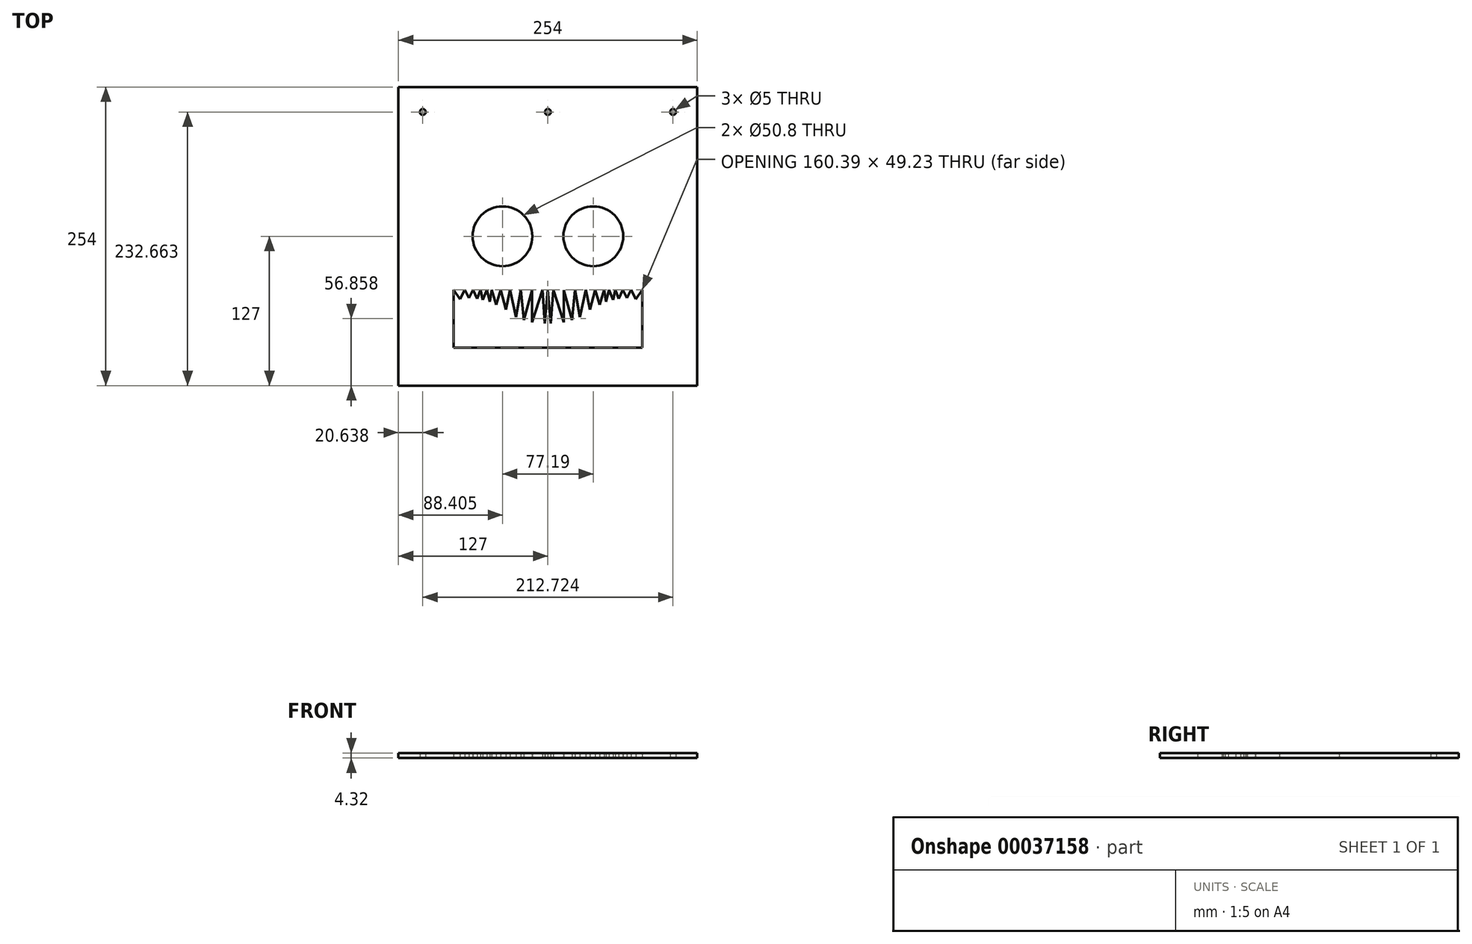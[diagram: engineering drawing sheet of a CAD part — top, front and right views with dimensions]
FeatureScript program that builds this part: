
annotation { "Feature Type Name" : "Feature", "Feature Type Description" : "" }
export const myFeature = defineFeature(function(context is Context, id is Id, definition is map)
    precondition{}
    {
        {
            var Q0;
            Q0=qCreatedBy(makeId("Top.planeOp"),FACE);
            var sketch = newSketch(context, id + "F0", { "sketchPlane" : qUnion([Q0])});
            skLineSegment(sketch, "E0.rect.bottom", {"start": v(127, 127) * mm, "end": v(-127, 127) * mm});
            skLineSegment(sketch, "E0.rect.top", {"start": v(127, -127) * mm, "end": v(-127, -127) * mm});
            skLineSegment(sketch, "E0.rect.left", {"start": v(127, 127) * mm, "end": v(127, -127) * mm});
            skLineSegment(sketch, "E0.rect.right", {"start": v(-127, 127) * mm, "end": v(-127, -127) * mm});
            skPoint(sketch, "E0.rect.middle", {"position": v(0, 0) * mm});
            skPoint(sketch, "E1.endSnap0", {"position": v(0, 127) * mm});
            skCircle(sketch, "E2", {"center": v(0, 105.66) * mm, "radius": 2.5 * mm});
            skCircle(sketch, "E3.MirrorC", {"center": v(-106.36, 105.66) * mm, "radius": 2.5 * mm});
            skCircle(sketch, "E4.MirrorC", {"center": v(106.36, 105.66) * mm, "radius": 2.5 * mm});
            skCircle(sketch, "E5", {"center": v(-38.6, 0) * mm, "radius": 25.4 * mm});
            skCircle(sketch, "E6.MirrorC", {"center": v(38.6, 0) * mm, "radius": 25.4 * mm});
            skLineSegment(sketch, "E7.top", {"start": v(0, -94.75) * mm, "end": v(-80.2, -94.75) * mm});
            skLineSegment(sketch, "E7.left", {"start": v(0, -45.53) * mm, "end": v(0, -94.75) * mm});
            skLineSegment(sketch, "E7.right", {"start": v(-80.2, -45.53) * mm, "end": v(-80.2, -94.75) * mm});
            skLineSegment(sketch, "E8.MirrorCS", {"start": v(80.2, -45.53) * mm, "end": v(80.2, -94.75) * mm});
            skLineSegment(sketch, "E9.MirrorCS", {"start": v(0, -94.75) * mm, "end": v(80.2, -94.75) * mm});
            skLineSegment(sketch, "E10", {"start": v(-80.2, -45.53) * mm, "end": v(-74.65, -53.39) * mm});
            skLineSegment(sketch, "E11", {"start": v(-74.65, -53.39) * mm, "end": v(-70.72, -45.53) * mm});
            skLineSegment(sketch, "E12", {"start": v(-70.72, -45.53) * mm, "end": v(-67.25, -52.7) * mm});
            skLineSegment(sketch, "E13", {"start": v(-67.25, -52.7) * mm, "end": v(-63.79, -45.53) * mm});
            skLineSegment(sketch, "E14", {"start": v(-63.79, -45.53) * mm, "end": v(-60.09, -53.16) * mm});
            skLineSegment(sketch, "E15", {"start": v(-60.09, -53.16) * mm, "end": v(-57.32, -45.53) * mm});
            skLineSegment(sketch, "E16", {"start": v(-57.32, -45.53) * mm, "end": v(-55.47, -54.08) * mm});
            skLineSegment(sketch, "E17", {"start": v(-55.47, -54.08) * mm, "end": v(-51.77, -45.53) * mm});
            skLineSegment(sketch, "E18", {"start": v(-51.77, -45.53) * mm, "end": v(-49.46, -55.7) * mm});
            skLineSegment(sketch, "E19", {"start": v(-49.46, -55.7) * mm, "end": v(-47.84, -45.53) * mm});
            skLineSegment(sketch, "E20", {"start": v(-47.84, -45.53) * mm, "end": v(-43.91, -58.24) * mm});
            skLineSegment(sketch, "E21", {"start": v(-43.91, -58.24) * mm, "end": v(-40.1, -45.53) * mm});
            skLineSegment(sketch, "E22", {"start": v(-40.1, -45.53) * mm, "end": v(-35.6, -62.4) * mm});
            skLineSegment(sketch, "E23", {"start": v(-35.6, -62.4) * mm, "end": v(-32.36, -45.53) * mm});
            skLineSegment(sketch, "E24", {"start": v(-32.36, -45.53) * mm, "end": v(-27.27, -68.87) * mm});
            skLineSegment(sketch, "E25", {"start": v(-27.27, -68.87) * mm, "end": v(-23.11, -45.53) * mm});
            skLineSegment(sketch, "E26", {"start": v(-23.11, -45.53) * mm, "end": v(-20.57, -71.18) * mm});
            skLineSegment(sketch, "E27", {"start": v(-20.57, -71.18) * mm, "end": v(-13.4, -45.76) * mm});
            skLineSegment(sketch, "E28", {"start": v(-13.4, -45.76) * mm, "end": v(-13.4, -73.03) * mm});
            skLineSegment(sketch, "E29", {"start": v(-13.4, -73.03) * mm, "end": v(-4.62, -45.53) * mm});
            skLineSegment(sketch, "E30", {"start": v(-4.62, -45.53) * mm, "end": v(-2.54, -74.19) * mm});
            skLineSegment(sketch, "E31", {"start": v(-2.54, -74.19) * mm, "end": v(0, -45.53) * mm});
            skLineSegment(sketch, "E32.MirrorCS", {"start": v(2.54, -74.19) * mm, "end": v(0, -45.53) * mm});
            skLineSegment(sketch, "E33.MirrorCS", {"start": v(4.62, -45.53) * mm, "end": v(2.54, -74.19) * mm});
            skLineSegment(sketch, "E34.MirrorCS", {"start": v(13.4, -73.03) * mm, "end": v(4.62, -45.53) * mm});
            skLineSegment(sketch, "E35.MirrorCS", {"start": v(13.4, -45.76) * mm, "end": v(13.4, -73.03) * mm});
            skLineSegment(sketch, "E36.MirrorCS", {"start": v(20.57, -71.18) * mm, "end": v(13.4, -45.76) * mm});
            skLineSegment(sketch, "E37.MirrorCS", {"start": v(23.11, -45.53) * mm, "end": v(20.57, -71.18) * mm});
            skLineSegment(sketch, "E38.MirrorCS", {"start": v(27.27, -68.87) * mm, "end": v(23.11, -45.53) * mm});
            skLineSegment(sketch, "E39.MirrorCS", {"start": v(32.36, -45.53) * mm, "end": v(27.27, -68.87) * mm});
            skLineSegment(sketch, "E40.MirrorCS", {"start": v(35.6, -62.4) * mm, "end": v(32.36, -45.53) * mm});
            skLineSegment(sketch, "E41.MirrorCS", {"start": v(40.1, -45.53) * mm, "end": v(35.6, -62.4) * mm});
            skLineSegment(sketch, "E42.MirrorCS", {"start": v(43.91, -58.24) * mm, "end": v(40.1, -45.53) * mm});
            skLineSegment(sketch, "E43.MirrorCS", {"start": v(47.84, -45.53) * mm, "end": v(43.91, -58.24) * mm});
            skLineSegment(sketch, "E44.MirrorCS", {"start": v(49.46, -55.7) * mm, "end": v(47.84, -45.53) * mm});
            skLineSegment(sketch, "E45.MirrorCS", {"start": v(51.77, -45.53) * mm, "end": v(49.46, -55.7) * mm});
            skLineSegment(sketch, "E46.MirrorCS", {"start": v(55.47, -54.08) * mm, "end": v(51.77, -45.53) * mm});
            skLineSegment(sketch, "E47.MirrorCS", {"start": v(57.32, -45.53) * mm, "end": v(55.47, -54.08) * mm});
            skLineSegment(sketch, "E48.MirrorCS", {"start": v(60.09, -53.16) * mm, "end": v(57.32, -45.53) * mm});
            skLineSegment(sketch, "E49.MirrorCS", {"start": v(63.79, -45.53) * mm, "end": v(60.09, -53.16) * mm});
            skLineSegment(sketch, "E50.MirrorCS", {"start": v(67.25, -52.7) * mm, "end": v(63.79, -45.53) * mm});
            skLineSegment(sketch, "E51.MirrorCS", {"start": v(70.72, -45.53) * mm, "end": v(67.25, -52.7) * mm});
            skLineSegment(sketch, "E52.MirrorCS", {"start": v(74.65, -53.39) * mm, "end": v(70.72, -45.53) * mm});
            skLineSegment(sketch, "E53.MirrorCS", {"start": v(80.2, -45.53) * mm, "end": v(74.65, -53.39) * mm});
            skSolve(sketch);
        }
        {
            var Q0;
            Q0=makeQuery(id+"F0.imprint","IMPRINT",FACE,{"disambiguationData":[TD([[makeQuery(id+"F0.imprint","IMPRINT",EDGE,{"derivedFrom":sQuery(id+"F0.wireOp",EDGE,"E0.rect.bottom")}),1.0]])]});
            extrude(context, id + "F1", {"entities" : qUnion([Q0]), "depth" : 4.32 * mm});
        }
        {
            var Q0;
            Q0=makeQuery(id+"F0.imprint","IMPRINT",FACE,{"disambiguationData":[TD([[makeQuery(id+"F0.imprint","IMPRINT",EDGE,{"derivedFrom":sQuery(id+"F0.wireOp",EDGE,"E0.rect.bottom")}),1.0]])]});
            extrude(context, id + "F2", {"entities" : qUnion([Q0]), "operationType" : NewBodyOperationType.ADD, "depth" : 4.32 * mm});
        }
    });
